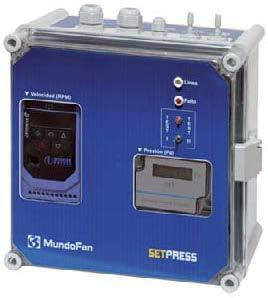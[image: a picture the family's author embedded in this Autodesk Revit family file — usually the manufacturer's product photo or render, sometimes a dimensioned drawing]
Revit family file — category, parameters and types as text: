
# Revit family: SETPRESS-075_VE10805
name_source: partatom
category: Aparatos eléctricos
revit_build: Autodesk Revit 2016 (Build: 20150220_1215(x64)
units: mm (PartAtom-declared; Revit-internal decimal feet)

## family parameters
Compartido = No
Corte con vacíos al cargar = No
Cota de conector redondo = Diámetro de uso
Mantener orientación de anotación = No
Número OmniClass = 23.80.00.00
Punto de cálculo de habitación = No
Se basa en plano de trabajo = No
Siempre vertical = Sí
Tipo de pieza = Caja de conexiones
Título OmniClass = Electric Power and Lighting

## types (1)
- SETPRESS
    Alimentación = 230Vac monofásico
    Corriente = 4,3 A
    Costo = 0 $
    Código de montaje = VE10805
    Descripción = CONTROL EFICIENCIA ENERGETICA PARA VENTILADORES
    Dimensiones máx. = 270x300x170 mm
    Fabricante = SALVADOR ESCODA
    Imagen de tipo = setpress.jpg
    Leds = linea / fallo
    Modelo = SETPRESS 0,75 kW
    Normativas = UNE-EN 12101-6
    Potencia = 0,75 kW
    Regulación = Mediante sonda analógica de presión
    Salida = 230Vac trifásico
    URL = www.salvadorescoda.com
    Visualización = frecuencia (Hz) y presión (Pa)
